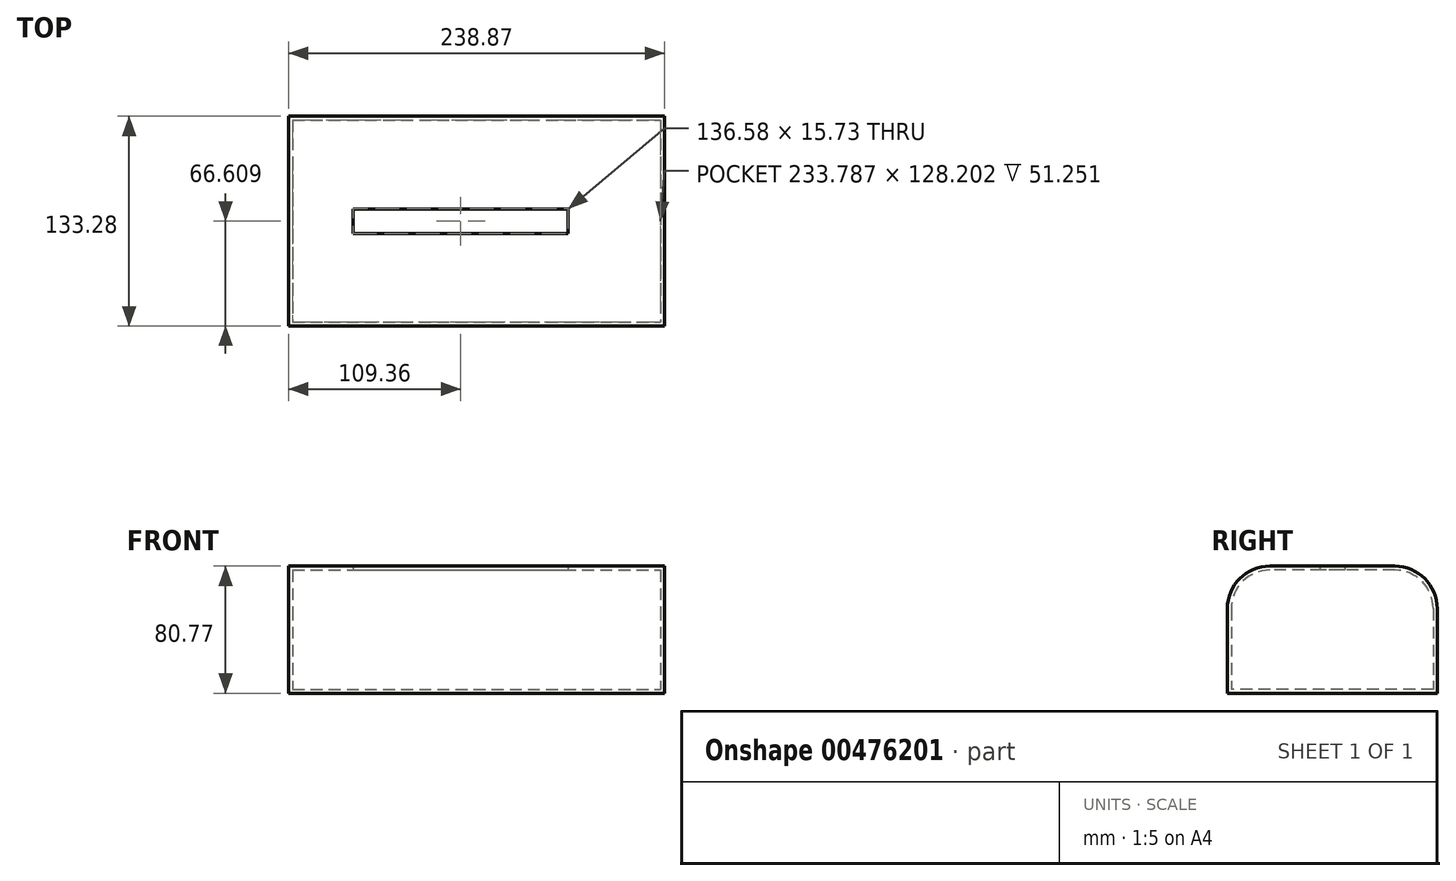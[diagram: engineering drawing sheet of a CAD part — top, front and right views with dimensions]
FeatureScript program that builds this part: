
annotation { "Feature Type Name" : "Feature", "Feature Type Description" : "" }
export const myFeature = defineFeature(function(context is Context, id is Id, definition is map)
    precondition{}
    {
        {
            var Q0;
            Q0=qCreatedBy(makeId("Top.planeOp"),FACE);
            var sketch = newSketch(context, id + "F0", { "sketchPlane" : qUnion([Q0])});
            skLineSegment(sketch, "E0.bottom", {"start": v(-116.53, 67.45) * mm, "end": v(122.34, 67.45) * mm});
            skLineSegment(sketch, "E0.top", {"start": v(-116.53, -65.83) * mm, "end": v(122.34, -65.83) * mm});
            skLineSegment(sketch, "E0.left", {"start": v(-116.53, 67.45) * mm, "end": v(-116.53, -65.83) * mm});
            skLineSegment(sketch, "E0.right", {"start": v(122.34, 67.45) * mm, "end": v(122.34, -65.83) * mm});
            skSolve(sketch);
        }
        {
            var Q0;
            Q0=makeQuery(id+"F0.imprint","IMPRINT",FACE,{"disambiguationData":[TD([[makeQuery(id+"F0.imprint","IMPRINT",EDGE,{"derivedFrom":sQuery(id+"F0.wireOp",EDGE,"E0.bottom")}),-1.0]])]});
            extrude(context, id + "F1", {"entities" : qUnion([Q0]), "depth" : 80.77 * mm});
        }
        {
            var Q0;
            Q0=makeQuery(id+"F1.opExtrude","CAP_EDGE",EDGE,{"disambiguationData":[OSD([sQuery(id+"F0.wireOp",EDGE,"E0.top")])],"isStart":false});
            var Q1;
            Q1=makeQuery(id+"F1.opExtrude","CAP_EDGE",EDGE,{"disambiguationData":[OSD([sQuery(id+"F0.wireOp",EDGE,"E0.bottom")])],"isStart":false});
            fillet(context, id + "F2", {"entities" : qUnion([Q0, Q1]), "radius" : 26.98 * mm, "tangentPropagation" : true, "allowEdgeOverflow" : false});
        }
        {
            var Q0;
            Q0=makeQuery(id+"F1.opExtrude","CAP_FACE",FACE,{"disambiguationData":[OSD([sQuery(id+"F0.wireOp",EDGE,"E0.bottom"),sQuery(id+"F0.wireOp",EDGE,"E0.top"),sQuery(id+"F0.wireOp",EDGE,"E0.left"),sQuery(id+"F0.wireOp",EDGE,"E0.right")])],"isStart":false});
            var sketch = newSketch(context, id + "F3", { "sketchPlane" : qUnion([Q0])});
            skLineSegment(sketch, "E1.bottom", {"start": v(-75.46, 8.64) * mm, "end": v(61.12, 8.64) * mm});
            skLineSegment(sketch, "E1.top", {"start": v(-75.46, -7.09) * mm, "end": v(61.12, -7.09) * mm});
            skLineSegment(sketch, "E1.left", {"start": v(-75.46, 8.64) * mm, "end": v(-75.46, -7.09) * mm});
            skLineSegment(sketch, "E1.right", {"start": v(61.12, 8.64) * mm, "end": v(61.12, -7.09) * mm});
            skSolve(sketch);
        }
        {
            var Q0;
            Q0=makeQuery(id+"F3.imprint","IMPRINT",FACE,{"disambiguationData":[TD([[makeQuery(id+"F3.imprint","IMPRINT",EDGE,{"derivedFrom":sQuery(id+"F3.wireOp",EDGE,"E1.bottom")}),-1.0]])]});
            extrude(context, id + "F4", {"entities" : qUnion([Q0]), "operationType" : NewBodyOperationType.ADD, "depth" : 15.75 * mm});
        }
        {
            var Q0;
            Q0=makeQuery(id+"F4.opExtrude","SWEPT_FACE",FACE,{"disambiguationData":[OSD([sQuery(id+"F3.wireOp",EDGE,"E1.top")])]});
            var Q1;
            Q1=makeQuery(id+"F4.opExtrude","SWEPT_FACE",FACE,{"disambiguationData":[OSD([sQuery(id+"F3.wireOp",EDGE,"E1.right")])]});
            var Q2;
            Q2=makeQuery(id+"F4.opExtrude","CAP_FACE",FACE,{"disambiguationData":[OSD([sQuery(id+"F3.wireOp",EDGE,"E1.bottom"),sQuery(id+"F3.wireOp",EDGE,"E1.top"),sQuery(id+"F3.wireOp",EDGE,"E1.left"),sQuery(id+"F3.wireOp",EDGE,"E1.right")])],"isStart":false});
            var Q3;
            Q3=makeQuery(id+"F4.opExtrude","SWEPT_FACE",FACE,{"disambiguationData":[OSD([sQuery(id+"F3.wireOp",EDGE,"E1.bottom")])]});
            var Q4;
            Q4=makeQuery(id+"F4.opExtrude","SWEPT_FACE",FACE,{"disambiguationData":[OSD([sQuery(id+"F3.wireOp",EDGE,"E1.left")])]});
            shell(context, id + "F5", {"entities" : qUnion([Q0, Q1, Q2, Q3, Q4]), "thickness" : 2.54 * mm});
        }
    });
